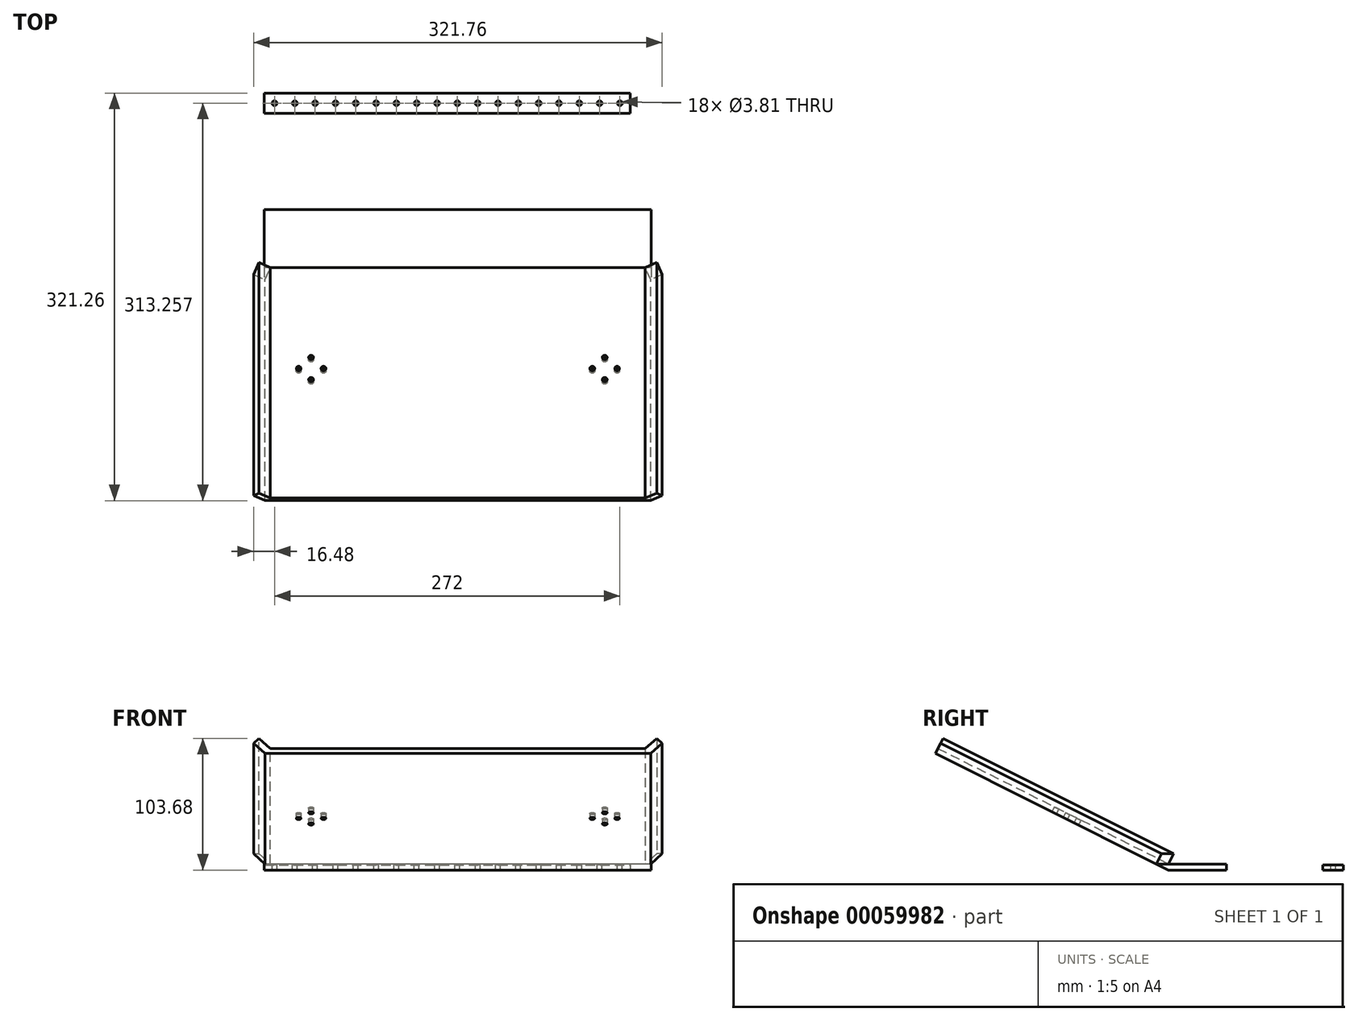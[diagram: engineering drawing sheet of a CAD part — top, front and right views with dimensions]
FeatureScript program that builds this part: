
annotation { "Feature Type Name" : "Feature", "Feature Type Description" : "" }
export const myFeature = defineFeature(function(context is Context, id is Id, definition is map)
    precondition{}
    {
        {
            var Q0;
            Q0=qCreatedBy(makeId("Right.planeOp"),FACE);
            var sketch = newSketch(context, id + "F0", { "sketchPlane" : qUnion([Q0])});
            skLineSegment(sketch, "E0.bottom", {"start": v(0, 0) * mm, "end": v(-45.72, 0) * mm});
            skLineSegment(sketch, "E0.top", {"start": v(0, 4.76) * mm, "end": v(-45.72, 4.76) * mm});
            skLineSegment(sketch, "E0.left", {"start": v(0, 0) * mm, "end": v(0, 4.76) * mm});
            skLineSegment(sketch, "E0.right", {"start": v(-45.72, 0) * mm, "end": v(-45.72, 4.76) * mm});
            skLineSegment(sketch, "E1", {"start": v(-45.72, 0) * mm, "end": v(-229.37, 91.84) * mm});
            skLineSegment(sketch, "E2", {"start": v(-229.37, 91.84) * mm, "end": v(-227.46, 95.65) * mm});
            skLineSegment(sketch, "E3", {"start": v(-227.46, 95.65) * mm, "end": v(-45.72, 4.76) * mm});
            skSolve(sketch);
        }
        {
            var Q0;
            Q0 = qSketchRegion(id + "F0", true);
            extrude(context, id + "F1", {"entities" : qUnion([Q0]), "depth" : 304.8 * mm});
        }
        {
            var Q0;
            Q0=makeQuery(id+"F1.opExtrude","CAP_EDGE",EDGE,{"disambiguationData":[OSD([sQuery(id+"F0.wireOp",EDGE,"E3")])],"isStart":false});
            var Q1;
            Q1=makeQuery(id+"F1.opExtrude","CAP_EDGE",EDGE,{"disambiguationData":[OSD([sQuery(id+"F0.wireOp",EDGE,"E3")])],"isStart":true});
            chamfer(context, id + "F2", {"entities" : qUnion([Q0, Q1]), "chamferType" : ChamferType.OFFSET_ANGLE, "width" : 4.76 * mm, "oppositeDirection" : false, "angle" : 45 * degree, "tangentPropagation" : true});
        }
        {
            var Q0;
            {var subQ0=sQuery(id+"F0.wireOp",EDGE,"E3");Q0=makeQuery(id+"F2.opChamfer","BLEND_FACE",FACE,{"disambiguationData":[OSD([subQ0]),TDD([makeQuery(id+"F1.opExtrude","CAP_EDGE",EDGE,{"disambiguationData":[OSD([subQ0])],"isStart":false})])]});}
            extrude(context, id + "F3", {"entities" : qUnion([Q0]), "operationType" : NewBodyOperationType.ADD, "depth" : 12.7 * mm});
        }
        {
            var Q0;
            {var subQ0=sQuery(id+"F0.wireOp",EDGE,"E3");Q0=makeQuery(id+"F2.opChamfer","BLEND_FACE",FACE,{"disambiguationData":[OSD([subQ0]),TDD([makeQuery(id+"F1.opExtrude","CAP_EDGE",EDGE,{"disambiguationData":[OSD([subQ0])],"isStart":true})])]});}
            extrude(context, id + "F4", {"entities" : qUnion([Q0]), "operationType" : NewBodyOperationType.ADD, "depth" : 12.7 * mm});
        }
        {
            var Q0;
            Q0=qCreatedBy(makeId("Top.planeOp"),FACE);
            var sketch = newSketch(context, id + "F5", { "sketchPlane" : qUnion([Q0])});
            skLineSegment(sketch, "E4.bottom", {"start": v(0, 75.89) * mm, "end": v(288, 75.89) * mm});
            skLineSegment(sketch, "E4.top", {"start": v(0, 91.89) * mm, "end": v(288, 91.89) * mm});
            skLineSegment(sketch, "E4.left", {"start": v(0, 75.89) * mm, "end": v(0, 91.89) * mm});
            skLineSegment(sketch, "E4.right", {"start": v(288, 75.89) * mm, "end": v(288, 91.89) * mm});
            skSolve(sketch);
        }
        {
            var Q0;
            Q0=makeQuery(id+"F5.imprint","IMPRINT",FACE,{"disambiguationData":[TD([[makeQuery(id+"F5.imprint","IMPRINT",EDGE,{"derivedFrom":sQuery(id+"F5.wireOp",EDGE,"E4.bottom")}),1.0]])]});
            extrude(context, id + "F6", {"entities" : qUnion([Q0]), "depth" : 4 * mm});
        }
        {
            var Q0;
            Q0=makeQuery(id+"F6.opExtrude","CAP_FACE",FACE,{"disambiguationData":[OSD([sQuery(id+"F5.wireOp",EDGE,"E4.bottom"),sQuery(id+"F5.wireOp",EDGE,"E4.top"),sQuery(id+"F5.wireOp",EDGE,"E4.left"),sQuery(id+"F5.wireOp",EDGE,"E4.right")])],"isStart":false});
            var sketch = newSketch(context, id + "F7", { "sketchPlane" : qUnion([Q0])});
            skCircle(sketch, "E5", {"center": v(8, 83.89) * mm, "radius": 1.9 * mm});
            skPoint(sketch, "E5.centerSnap0", {"position": v(0, 83.89) * mm});
            skCircle(sketch, "E6.1.0.0", {"center": v(24, 83.89) * mm, "radius": 1.9 * mm});
            skCircle(sketch, "E6.2.0.0", {"center": v(40, 83.89) * mm, "radius": 1.9 * mm});
            skCircle(sketch, "E6.3.0.0", {"center": v(56, 83.89) * mm, "radius": 1.9 * mm});
            skCircle(sketch, "E6.4.0.0", {"center": v(72, 83.89) * mm, "radius": 1.9 * mm});
            skCircle(sketch, "E6.5.0.0", {"center": v(88, 83.89) * mm, "radius": 1.9 * mm});
            skCircle(sketch, "E6.6.0.0", {"center": v(104, 83.89) * mm, "radius": 1.9 * mm});
            skCircle(sketch, "E6.7.0.0", {"center": v(120, 83.89) * mm, "radius": 1.9 * mm});
            skCircle(sketch, "E6.8.0.0", {"center": v(136, 83.89) * mm, "radius": 1.9 * mm});
            skCircle(sketch, "E6.9.0.0", {"center": v(152, 83.89) * mm, "radius": 1.9 * mm});
            skCircle(sketch, "E6.10.0.0", {"center": v(168, 83.89) * mm, "radius": 1.9 * mm});
            skCircle(sketch, "E6.11.0.0", {"center": v(184, 83.89) * mm, "radius": 1.9 * mm});
            skCircle(sketch, "E6.12.0.0", {"center": v(200, 83.89) * mm, "radius": 1.9 * mm});
            skCircle(sketch, "E6.13.0.0", {"center": v(216, 83.89) * mm, "radius": 1.9 * mm});
            skCircle(sketch, "E6.14.0.0", {"center": v(232, 83.89) * mm, "radius": 1.9 * mm});
            skCircle(sketch, "E6.15.0.0", {"center": v(248, 83.89) * mm, "radius": 1.9 * mm});
            skCircle(sketch, "E6.16.0.0", {"center": v(264, 83.89) * mm, "radius": 1.9 * mm});
            skCircle(sketch, "E6.17.0.0", {"center": v(280, 83.89) * mm, "radius": 1.9 * mm});
            skLineSegment(sketch, "E6.direction1", {"start": v(8, 83.89) * mm, "end": v(24, 83.89) * mm, "construction": true});
            skSolve(sketch);
        }
        {
            var Q0;
            Q0 = qSketchRegion(id + "F7", true);
            extrude(context, id + "F8", {"entities" : qUnion([Q0]), "operationType" : NewBodyOperationType.REMOVE, "endBound" : BoundingType.UP_TO_NEXT, "oppositeDirection" : true, "depth" : 25.4 * mm});
        }
        {
            var Q0;
            Q0=makeQuery(id+"F1.opExtrude","SWEPT_FACE",FACE,{"disambiguationData":[OSD([sQuery(id+"F0.wireOp",EDGE,"E1")])]});
            var sketch = newSketch(context, id + "F9", { "sketchPlane" : qUnion([Q0])});
            skCircle(sketch, "E7", {"center": v(36.77, 122.14) * mm, "radius": 1.9 * mm});
            skCircle(sketch, "E8", {"center": v(36.77, 131.92) * mm, "radius": 9.78 * mm, "construction": true});
            skLineSegment(sketch, "E9", {"start": v(36.77, 131.92) * mm, "end": v(36.77, 122.14) * mm, "construction": true});
            skCircle(sketch, "E10.1.0", {"center": v(46.55, 131.92) * mm, "radius": 1.9 * mm});
            skCircle(sketch, "E10.2.0", {"center": v(36.77, 141.7) * mm, "radius": 1.9 * mm});
            skCircle(sketch, "E10.3.0", {"center": v(26.99, 131.92) * mm, "radius": 1.9 * mm});
            skLineSegment(sketch, "E11", {"start": v(152.4, 40.9) * mm, "end": v(152.4, 246.22) * mm, "construction": true});
            skPoint(sketch, "E12.MirrorP", {"position": v(268.03, 131.92) * mm});
            skCircle(sketch, "E13.MirrorC", {"center": v(277.81, 131.92) * mm, "radius": 1.9 * mm});
            skCircle(sketch, "E14.MirrorC", {"center": v(268.03, 131.92) * mm, "radius": 9.78 * mm, "construction": true});
            skLineSegment(sketch, "E15.MirrorCS", {"start": v(268.03, 131.92) * mm, "end": v(268.03, 122.14) * mm, "construction": true});
            skCircle(sketch, "E16.MirrorC", {"center": v(258.25, 131.92) * mm, "radius": 1.9 * mm});
            skCircle(sketch, "E17.MirrorC", {"center": v(268.03, 122.14) * mm, "radius": 1.9 * mm});
            skCircle(sketch, "E18.MirrorC", {"center": v(268.03, 141.7) * mm, "radius": 1.9 * mm});
            skSolve(sketch);
        }
        {
            var Q0;
            Q0 = qSketchRegion(id + "F9", true);
            extrude(context, id + "F10", {"entities" : qUnion([Q0]), "operationType" : NewBodyOperationType.REMOVE, "endBound" : BoundingType.UP_TO_NEXT, "oppositeDirection" : true, "depth" : 25.4 * mm});
        }
    });
